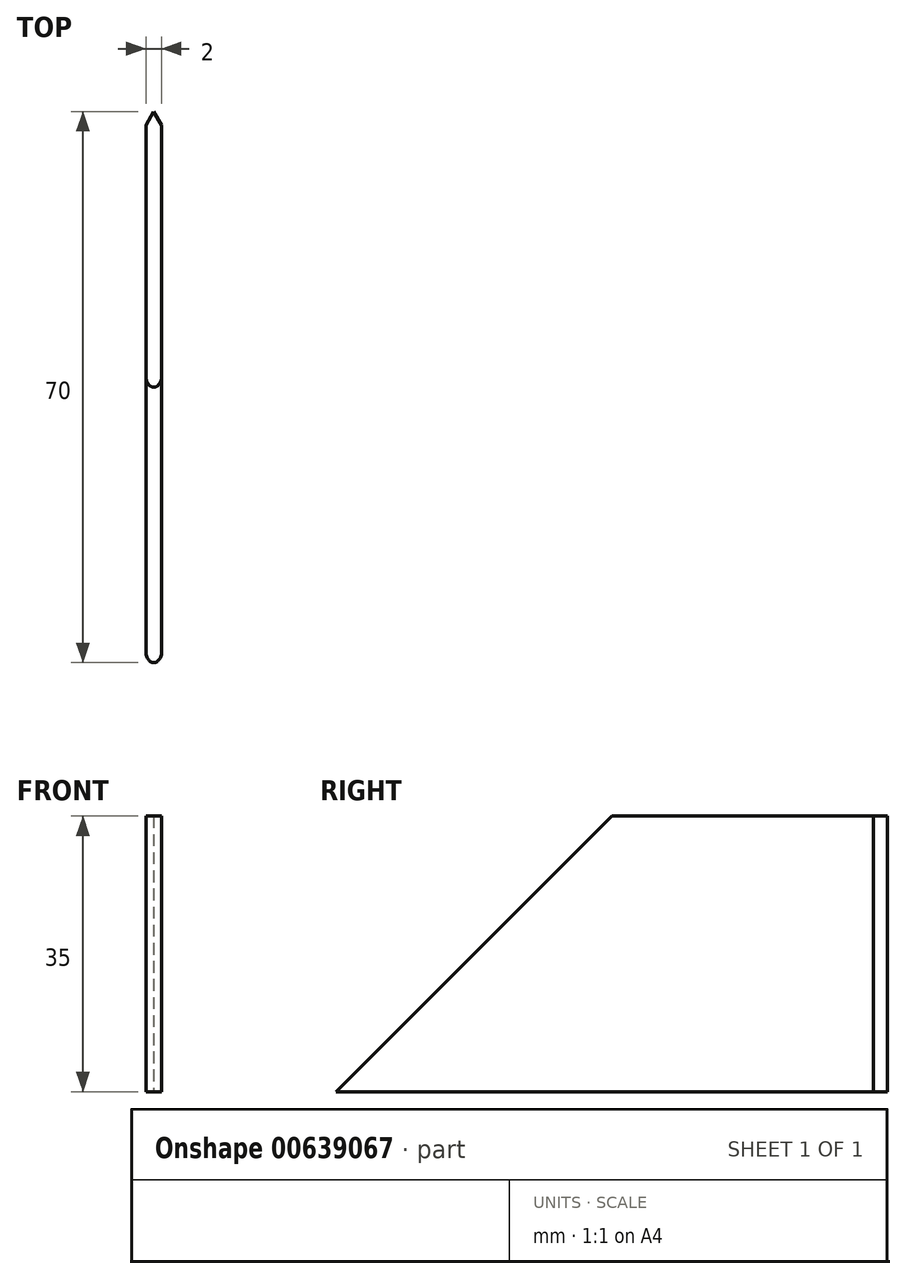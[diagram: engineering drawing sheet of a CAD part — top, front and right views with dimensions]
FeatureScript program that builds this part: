
annotation { "Feature Type Name" : "Feature", "Feature Type Description" : "" }
export const myFeature = defineFeature(function(context is Context, id is Id, definition is map)
    precondition{}
    {
        {
            var Q0;
            Q0=qCreatedBy(makeId("Right.planeOp"),FACE);
            var sketch = newSketch(context, id + "F0", { "sketchPlane" : qUnion([Q0])});
            skLineSegment(sketch, "E0", {"start": v(0, 0) * mm, "end": v(-70, 0) * mm});
            skLineSegment(sketch, "E1", {"start": v(-70, 0) * mm, "end": v(-35, 35) * mm});
            skLineSegment(sketch, "E2", {"start": v(-35, 35) * mm, "end": v(0, 35) * mm});
            skLineSegment(sketch, "E3", {"start": v(0, 35) * mm, "end": v(0, 0) * mm});
            skLineSegment(sketch, "E4.bottom", {"start": v(-70, 0) * mm, "end": v(0, 0) * mm});
            skLineSegment(sketch, "E4.top", {"start": v(-70, -5) * mm, "end": v(0, -5) * mm});
            skLineSegment(sketch, "E4.left", {"start": v(-70, 0) * mm, "end": v(-70, -5) * mm});
            skLineSegment(sketch, "E4.right", {"start": v(0, 0) * mm, "end": v(0, -5) * mm});
            skSolve(sketch);
        }
        {
            var Q0;
            Q0=makeQuery(id+"F0.imprint","IMPRINT",FACE,{"disambiguationData":[TD([[makeQuery(id+"F0.imprint","IMPRINT",EDGE,{"derivedFrom":sQuery(id+"F0.wireOp",EDGE,"E1")}),-1.0]])]});
            var Q1;
            Q1=makeQuery(id+"F0.imprint","IMPRINT",FACE,{"disambiguationData":[TD([[makeQuery(id+"F0.imprint","IMPRINT",EDGE,{"derivedFrom":sQuery(id+"F0.wireOp",EDGE,"E4.bottom")}),-1.0]])]});
            extrude(context, id + "F1", {"entities" : qUnion([Q0, Q1]), "endBound" : BoundingType.SYMMETRIC, "depth" : 2 * mm, "offsetDistance" : 25 * mm});
        }
        {
            var Q0;
            Q0=makeQuery(id+"F1.opExtrude","CAP_EDGE",EDGE,{"disambiguationData":[OSD([sQuery(id+"F0.wireOp",EDGE,"E1")])],"isStart":false});
            fillet(context, id + "F2", {"entities" : qUnion([Q0]), "radius" : 1 * mm, "tangentPropagation" : true, "allowEdgeOverflow" : false});
        }
        {
            var Q0;
            Q0=makeQuery(id+"F1.opExtrude","CAP_EDGE",EDGE,{"disambiguationData":[OSD([sQuery(id+"F0.wireOp",EDGE,"E1")])],"isStart":true});
            fillet(context, id + "F3", {"entities" : qUnion([Q0]), "radius" : 1 * mm, "tangentPropagation" : true, "allowEdgeOverflow" : false});
        }
        {
            var Q0;
            Q0=qCreatedBy(makeId("Front.planeOp"),FACE);
            var sketch = newSketch(context, id + "F4", { "sketchPlane" : qUnion([Q0])});
            skLineSegment(sketch, "E5", {"start": v(0, 0) * mm, "end": v(0, -16.5) * mm});
            skCircle(sketch, "E6", {"center": v(0, -16.5) * mm, "radius": 16.5 * mm});
            skSolve(sketch);
        }
        {
            var Q0;
            Q0 = qSketchRegion(id + "F4", true);
            extrude(context, id + "F5", {"entities" : qUnion([Q0]), "operationType" : NewBodyOperationType.REMOVE, "endBound" : BoundingType.SYMMETRIC, "depth" : 150 * mm, "offsetDistance" : 25 * mm});
        }
        {
            var Q0;
            Q0=makeQuery(id+"F1.opExtrude","CAP_EDGE",EDGE,{"disambiguationData":[OSD([sQuery(id+"F0.wireOp",EDGE,"E3"),sQuery(id+"F0.wireOp",EDGE,"E4.right")])],"isStart":false});
            chamfer(context, id + "F6", {"entities" : qUnion([Q0]), "chamferType" : ChamferType.OFFSET_ANGLE, "width" : 1 * mm, "oppositeDirection" : false, "angle" : 60 * degree, "tangentPropagation" : true});
        }
        {
            var Q0;
            Q0=makeQuery(id+"F1.opExtrude","CAP_EDGE",EDGE,{"disambiguationData":[OSD([sQuery(id+"F0.wireOp",EDGE,"E3"),sQuery(id+"F0.wireOp",EDGE,"E4.right")])],"isStart":true});
            chamfer(context, id + "F7", {"entities" : qUnion([Q0]), "chamferType" : ChamferType.OFFSET_ANGLE, "width" : 1 * mm, "oppositeDirection" : true, "angle" : 60 * degree, "tangentPropagation" : true});
        }
    });
